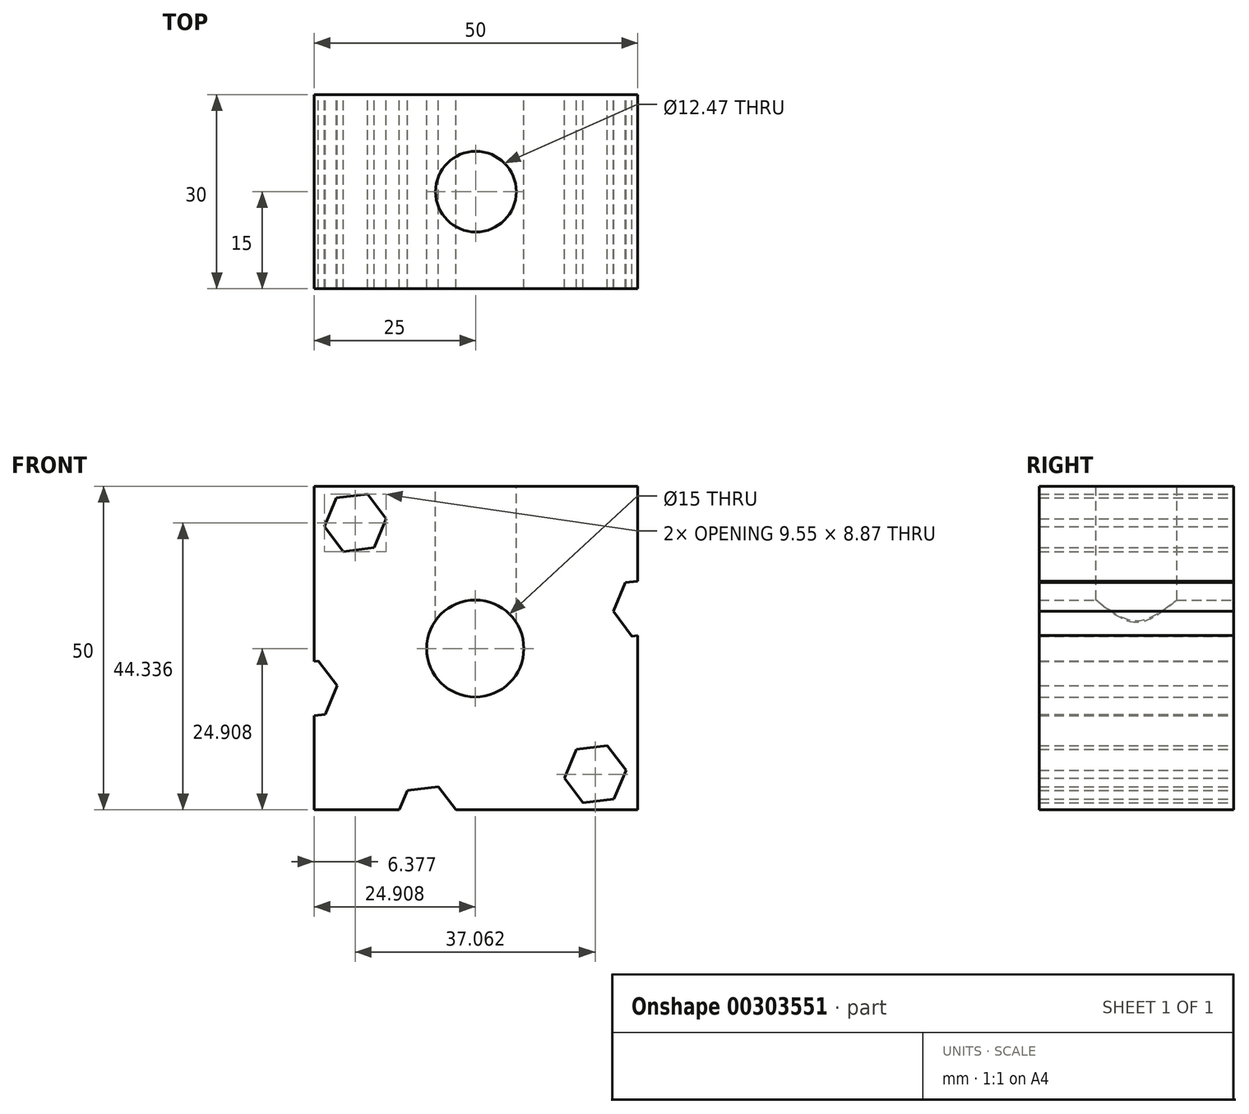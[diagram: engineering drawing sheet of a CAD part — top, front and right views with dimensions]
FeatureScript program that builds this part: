
annotation { "Feature Type Name" : "Feature", "Feature Type Description" : "" }
export const myFeature = defineFeature(function(context is Context, id is Id, definition is map)
    precondition{}
    {
        {
            var Q0;
            Q0=qCreatedBy(makeId("Front.planeOp"),FACE);
            var sketch = newSketch(context, id + "F0", { "sketchPlane" : qUnion([Q0])});
            skLineSegment(sketch, "E0.bottom", {"start": v(0, 0) * mm, "end": v(50, 0) * mm});
            skLineSegment(sketch, "E0.top", {"start": v(0, 50) * mm, "end": v(50, 50) * mm});
            skLineSegment(sketch, "E0.left", {"start": v(0, 0) * mm, "end": v(0, 50) * mm});
            skLineSegment(sketch, "E0.right", {"start": v(50, 0) * mm, "end": v(50, 50) * mm});
            skCircle(sketch, "E1", {"center": v(24.9, 24.9) * mm, "radius": 7.5 * mm});
            skPoint(sketch, "E1.centerSnap0", {"position": v(50, 25) * mm});
            skPoint(sketch, "E1.centerSnap1", {"position": v(25, 50) * mm});
            skCircle(sketch, "E2.cCircle", {"center": v(6.38, 44.34) * mm, "radius": 4.17 * mm, "construction": true});
            skLineSegment(sketch, "E2.0", {"start": v(11.15, 44.93) * mm, "end": v(9.28, 40.5) * mm});
            skLineSegment(sketch, "E2.1", {"start": v(9.28, 40.5) * mm, "end": v(4.5, 39.9) * mm});
            skLineSegment(sketch, "E2.2", {"start": v(4.5, 39.9) * mm, "end": v(1.6, 43.74) * mm});
            skLineSegment(sketch, "E2.3", {"start": v(1.6, 43.74) * mm, "end": v(3.47, 48.17) * mm});
            skLineSegment(sketch, "E2.4", {"start": v(3.47, 48.17) * mm, "end": v(8.25, 48.77) * mm});
            skLineSegment(sketch, "E2.5", {"start": v(8.25, 48.77) * mm, "end": v(11.15, 44.93) * mm});
            skPoint(sketch, "E2.0.midPoint", {"position": v(10.22, 42.72) * mm});
            skPoint(sketch, "E3.1.0", {"position": v(2.14, 21.09) * mm});
            skCircle(sketch, "E3.1.1", {"center": v(-1.18, 18.57) * mm, "radius": 4.17 * mm, "construction": true});
            skLineSegment(sketch, "E3.1.2", {"start": v(-4.09, 22.41) * mm, "end": v(0.69, 23) * mm});
            skLineSegment(sketch, "E3.1.3", {"start": v(-3.05, 14.14) * mm, "end": v(-5.96, 17.98) * mm});
            skLineSegment(sketch, "E3.1.4", {"start": v(3.6, 19.17) * mm, "end": v(1.72, 14.74) * mm});
            skLineSegment(sketch, "E3.1.5", {"start": v(-5.96, 17.98) * mm, "end": v(-4.09, 22.41) * mm});
            skLineSegment(sketch, "E3.1.6", {"start": v(1.72, 14.74) * mm, "end": v(-3.05, 14.14) * mm});
            skLineSegment(sketch, "E3.1.7", {"start": v(0.69, 23) * mm, "end": v(3.6, 19.17) * mm});
            skPoint(sketch, "E3.2.0", {"position": v(16.83, 3.28) * mm});
            skCircle(sketch, "E3.2.1", {"center": v(17.35, -0.85) * mm, "radius": 4.17 * mm, "construction": true});
            skLineSegment(sketch, "E3.2.2", {"start": v(12.57, -1.45) * mm, "end": v(14.44, 2.98) * mm});
            skLineSegment(sketch, "E3.2.3", {"start": v(20.25, -4.7) * mm, "end": v(15.48, -5.29) * mm});
            skLineSegment(sketch, "E3.2.4", {"start": v(19.22, 3.58) * mm, "end": v(22.12, -0.26) * mm});
            skLineSegment(sketch, "E3.2.5", {"start": v(15.48, -5.29) * mm, "end": v(12.57, -1.45) * mm});
            skLineSegment(sketch, "E3.2.6", {"start": v(22.12, -0.26) * mm, "end": v(20.25, -4.7) * mm});
            skLineSegment(sketch, "E3.2.7", {"start": v(14.44, 2.98) * mm, "end": v(19.22, 3.58) * mm});
            skPoint(sketch, "E3.3.0", {"position": v(39.6, 7.1) * mm});
            skCircle(sketch, "E3.3.1", {"center": v(43.44, 5.48) * mm, "radius": 4.17 * mm, "construction": true});
            skLineSegment(sketch, "E3.3.2", {"start": v(41.57, 1.05) * mm, "end": v(38.66, 4.88) * mm});
            skLineSegment(sketch, "E3.3.3", {"start": v(48.22, 6.08) * mm, "end": v(46.34, 1.64) * mm});
            skLineSegment(sketch, "E3.3.4", {"start": v(40.53, 9.32) * mm, "end": v(45.31, 9.92) * mm});
            skLineSegment(sketch, "E3.3.5", {"start": v(46.34, 1.64) * mm, "end": v(41.57, 1.05) * mm});
            skLineSegment(sketch, "E3.3.6", {"start": v(45.31, 9.92) * mm, "end": v(48.22, 6.08) * mm});
            skLineSegment(sketch, "E3.3.7", {"start": v(38.66, 4.88) * mm, "end": v(40.53, 9.32) * mm});
            skPoint(sketch, "E3.4.0", {"position": v(47.68, 28.73) * mm});
            skCircle(sketch, "E3.4.1", {"center": v(51, 31.24) * mm, "radius": 4.17 * mm, "construction": true});
            skLineSegment(sketch, "E3.4.2", {"start": v(53.9, 27.4) * mm, "end": v(49.13, 26.8) * mm});
            skLineSegment(sketch, "E3.4.3", {"start": v(52.87, 35.68) * mm, "end": v(55.77, 31.84) * mm});
            skLineSegment(sketch, "E3.4.4", {"start": v(46.22, 30.65) * mm, "end": v(48.1, 35.08) * mm});
            skLineSegment(sketch, "E3.4.5", {"start": v(55.77, 31.84) * mm, "end": v(53.9, 27.4) * mm});
            skLineSegment(sketch, "E3.4.6", {"start": v(48.1, 35.08) * mm, "end": v(52.87, 35.68) * mm});
            skLineSegment(sketch, "E3.4.7", {"start": v(49.13, 26.8) * mm, "end": v(46.22, 30.65) * mm});
            skLineSegment(sketch, "E3.anchor1", {"start": v(24.9, 24.9) * mm, "end": v(4.5, 39.9) * mm, "construction": true});
            skLineSegment(sketch, "E3.anchor2", {"start": v(24.9, 24.9) * mm, "end": v(48.1, 35.08) * mm, "construction": true});
            skSolve(sketch);
        }
        {
            var Q0;
            {var subQ14=sQuery(id+"F0.wireOp",EDGE,"E0.top");Q0=makeQuery(id+"F0.imprint","IMPRINT",FACE,{"disambiguationData":[TD([[makeQuery(id+"F0.imprint","IMPRINT",EDGE,{"derivedFrom":subQ14}),-1.0]])]});}
            extrude(context, id + "F1", {"entities" : qUnion([Q0]), "depth" : 30 * mm});
        }
        {
            var Q0;
            Q0=makeQuery(id+"F1.opExtrude","SWEPT_FACE",FACE,{"disambiguationData":[OSD([sQuery(id+"F0.wireOp",EDGE,"E0.top")])]});
            var sketch = newSketch(context, id + "F2", { "sketchPlane" : qUnion([Q0])});
            skCircle(sketch, "E4", {"center": v(25, -15) * mm, "radius": 6.23 * mm});
            skPoint(sketch, "E4.centerSnap0", {"position": v(25, 0) * mm});
            skPoint(sketch, "E4.centerSnap1", {"position": v(0, -15) * mm});
            skSolve(sketch);
        }
        {
            var Q0;
            Q0 = qSketchRegion(id + "F2", true);
            extrude(context, id + "F3", {"entities" : qUnion([Q0]), "operationType" : NewBodyOperationType.REMOVE, "oppositeDirection" : true, "depth" : 24.4 * mm});
        }
    });
